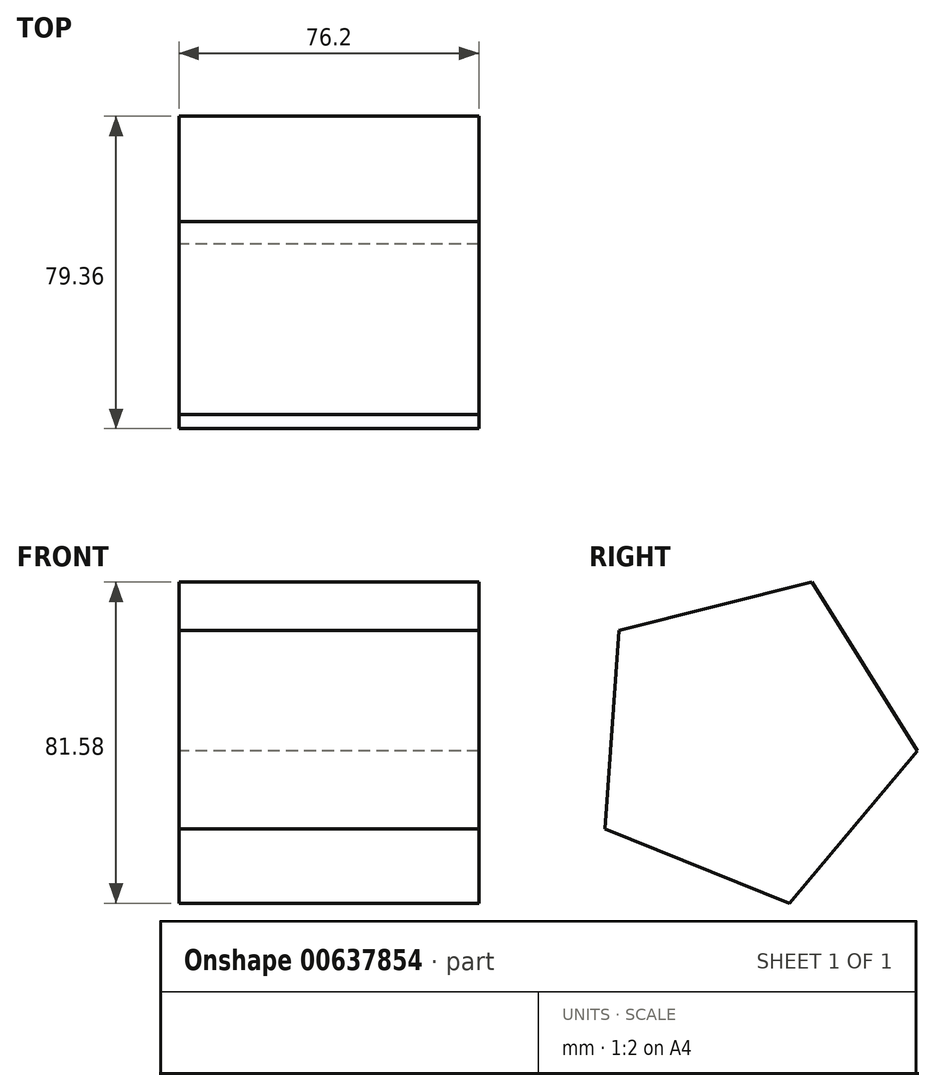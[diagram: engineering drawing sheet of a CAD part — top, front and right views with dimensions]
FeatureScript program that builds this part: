
annotation { "Feature Type Name" : "Feature", "Feature Type Description" : "" }
export const myFeature = defineFeature(function(context is Context, id is Id, definition is map)
    precondition{}
    {
        {
            var Q0;
            Q0=qCreatedBy(makeId("Right.planeOp"),FACE);
            var sketch = newSketch(context, id + "F0", { "sketchPlane" : qUnion([Q0])});
            skCircle(sketch, "E0.cCircle", {"center": v(0, 0) * mm, "radius": 34.78 * mm, "construction": true});
            skLineSegment(sketch, "E0.0", {"start": v(16.11, 39.86) * mm, "end": v(42.9, -3) * mm});
            skLineSegment(sketch, "E0.1", {"start": v(42.9, -3) * mm, "end": v(10.4, -41.72) * mm});
            skLineSegment(sketch, "E0.2", {"start": v(10.4, -41.72) * mm, "end": v(-36.47, -22.78) * mm});
            skLineSegment(sketch, "E0.3", {"start": v(-36.47, -22.78) * mm, "end": v(-32.93, 27.64) * mm});
            skLineSegment(sketch, "E0.4", {"start": v(-32.93, 27.64) * mm, "end": v(16.11, 39.86) * mm});
            skPoint(sketch, "E0.0.midPoint", {"position": v(29.5, 18.43) * mm});
            skSolve(sketch);
        }
        {
            var Q0;
            Q0=makeQuery(id+"F0.imprint","IMPRINT",FACE,{"disambiguationData":[TD([[makeQuery(id+"F0.imprint","IMPRINT",EDGE,{"derivedFrom":sQuery(id+"F0.wireOp",EDGE,"E0.0")}),-1.0]])]});
            extrude(context, id + "F1", {"entities" : qUnion([Q0]), "depth" : 76.2 * mm, "offsetDistance" : 25.4 * mm});
        }
    });
